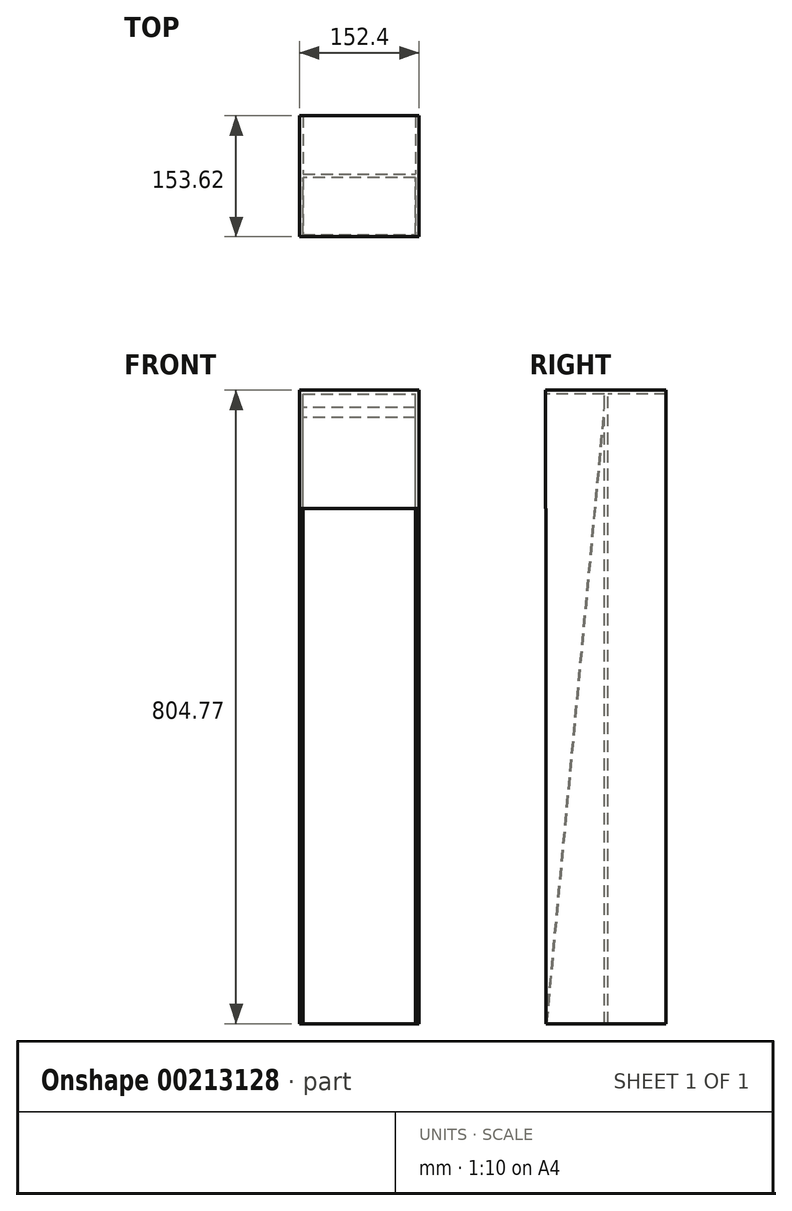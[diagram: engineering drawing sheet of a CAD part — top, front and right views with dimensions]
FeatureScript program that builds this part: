
annotation { "Feature Type Name" : "Feature", "Feature Type Description" : "" }
export const myFeature = defineFeature(function(context is Context, id is Id, definition is map)
    precondition{}
    {
        {
            var Q0;
            Q0=qCreatedBy(makeId("Top.planeOp"),FACE);
            var sketch = newSketch(context, id + "F0", { "sketchPlane" : qUnion([Q0])});
            skLineSegment(sketch, "E0.bottom", {"start": v(-76.2, -76.2) * mm, "end": v(-71.44, -76.2) * mm});
            skLineSegment(sketch, "E0.top", {"start": v(-76.2, 76.2) * mm, "end": v(-71.44, 76.2) * mm});
            skPoint(sketch, "E0.middle", {"position": v(0, 0) * mm});
            skLineSegment(sketch, "E1", {"start": v(-76.2, 76.2) * mm, "end": v(-76.2, -76.2) * mm});
            skLineSegment(sketch, "E2", {"start": v(-71.44, 76.2) * mm, "end": v(-71.44, 2.38) * mm});
            skLineSegment(sketch, "E3", {"start": v(76.2, 76.2) * mm, "end": v(76.2, -76.2) * mm});
            skLineSegment(sketch, "E4", {"start": v(71.44, 76.2) * mm, "end": v(71.44, 2.38) * mm});
            skLineSegment(sketch, "E5.trimOffspring", {"start": v(71.44, 76.2) * mm, "end": v(76.2, 76.2) * mm});
            skLineSegment(sketch, "E6.trimOffspring", {"start": v(71.44, -76.2) * mm, "end": v(76.2, -76.2) * mm});
            skLineSegment(sketch, "E7.0", {"start": v(-71.44, -2.38) * mm, "end": v(71.44, -2.38) * mm});
            skLineSegment(sketch, "E8.0", {"start": v(-71.44, 2.38) * mm, "end": v(71.44, 2.38) * mm});
            skLineSegment(sketch, "E9.trimOffspring", {"start": v(-71.44, -2.38) * mm, "end": v(-71.44, -76.2) * mm});
            skPoint(sketch, "E10.orphan", {"position": v(-71.44, 0) * mm});
            skPoint(sketch, "E11.end.orphan", {"position": v(71.44, 0) * mm});
            skLineSegment(sketch, "E12.trimOffspring", {"start": v(71.44, -2.38) * mm, "end": v(71.44, -76.2) * mm});
            skSolve(sketch);
        }
        {
            var Q0;
            Q0=qSketchRegion(id+"F0",true);
            extrude(context, id + "F1", {"entities" : qUnion([Q0]), "oppositeDirection" : true, "depth" : 800 * mm});
        }
        {
            var Q0;
            Q0=makeQuery(id+"F1.opExtrude","CAP_FACE",FACE,{"disambiguationData":[OSD([sQuery(id+"F0.wireOp",EDGE,"E0.bottom"),sQuery(id+"F0.wireOp",EDGE,"E0.top"),sQuery(id+"F0.wireOp",EDGE,"E0.left"),sQuery(id+"F0.wireOp",EDGE,"E0.right"),sQuery(id+"F0.wireOp",EDGE,"7a6f2c26-1c94-48de-b3ff-05aa15f8282d.0"),sQuery(id+"F0.wireOp",EDGE,"bf20579e-0ff9-4312-8226-057ec2ad24a0.0"),sQuery(id+"F0.wireOp",EDGE,"53fb2d3c-9874-4836-9c0b-58f450f03ea0.0"),sQuery(id+"F0.wireOp",EDGE,"893a7bcd-cfe5-4227-b07f-b4167a1dcdd1.0"),sQuery(id+"F0.wireOp",EDGE,"a6ffb2dd-69a9-4642-a933-3686e417fbb3.trimOffspring"),sQuery(id+"F0.wireOp",EDGE,"427ace22-e381-4167-ab2c-954d83dae6c8.trimOffspring"),sQuery(id+"F0.wireOp",EDGE,"ff942871-ae62-4c67-9aaa-94336091cfaf.trimOffspring"),sQuery(id+"F0.wireOp",EDGE,"886b6b8d-e2b2-4d8e-b841-3db4b76343a9.trimOffspring")])],"isStart":true});
            var sketch = newSketch(context, id + "F2", { "sketchPlane" : qUnion([Q0])});
            skLineSegment(sketch, "E13.bottom", {"start": v(-76.2, 76.2) * mm, "end": v(76.2, 76.2) * mm});
            skLineSegment(sketch, "E13.top", {"start": v(-76.2, -76.2) * mm, "end": v(76.2, -76.2) * mm});
            skLineSegment(sketch, "E13.left", {"start": v(-76.2, 76.2) * mm, "end": v(-76.2, -76.2) * mm});
            skLineSegment(sketch, "E13.right", {"start": v(76.2, 76.2) * mm, "end": v(76.2, -76.2) * mm});
            skPoint(sketch, "E13.middle", {"position": v(0, 0) * mm});
            skSolve(sketch);
        }
        {
            var Q0;
            Q0=qSketchRegion(id+"F2",true);
            extrude(context, id + "F3", {"entities" : qUnion([Q0]), "operationType" : NewBodyOperationType.ADD, "depth" : 4.76 * mm});
        }
        {
            var Q0;
            Q0=makeQuery(id+"F3.boolean.opBoolean","MERGE",FACE,{"derivedFrom":[makeQuery(id+"F1.opExtrude","SWEPT_FACE",FACE,{"disambiguationData":[OSD([sQuery(id+"F0.wireOp",EDGE,"E0.top")])]}),makeQuery(id+"F1.opExtrude","SWEPT_FACE",FACE,{"disambiguationData":[OSD([sQuery(id+"F0.wireOp",EDGE,"E5.trimOffspring")])]}),makeQuery(id+"F3.opExtrude","SWEPT_FACE",FACE,{"disambiguationData":[OSD([sQuery(id+"F2.wireOp",EDGE,"E13.bottom")])]})]});
            var sketch = newSketch(context, id + "F4", { "sketchPlane" : qUnion([Q0])});
            skLineSegment(sketch, "E14.top", {"start": v(-76.12, -3000.56) * mm, "end": v(75.55, -3000.56) * mm});
            skLineSegment(sketch, "E15", {"start": v(-76.2, -800) * mm, "end": v(76.2, -800) * mm});
            skLineSegment(sketch, "E16", {"start": v(-76.2, 4.76) * mm, "end": v(76.2, 4.76) * mm});
            skLineSegment(sketch, "E17", {"start": v(76.2, 4.76) * mm, "end": v(76.2, -800) * mm});
            skLineSegment(sketch, "E18", {"start": v(-76.2, -800) * mm, "end": v(-76.2, 4.76) * mm});
            skSolve(sketch);
        }
        {
            var Q0;
            Q0=qSketchRegion(id+"F4",true);
            extrude(context, id + "F5", {"entities" : qUnion([Q0]), "operationType" : NewBodyOperationType.ADD, "depth" : 3 / 406.4 * mm});
        }
        {
            var Q0;
            Q0=makeQuery(id+"F3.opExtrude","SWEPT_FACE",FACE,{"disambiguationData":[OSD([sQuery(id+"F2.wireOp",EDGE,"E13.top")])]});
            var sketch = newSketch(context, id + "F6", { "sketchPlane" : qUnion([Q0])});
            skLineSegment(sketch, "E19.bottom", {"start": v(-76.2, 4.76) * mm, "end": v(76.2, 4.76) * mm});
            skLineSegment(sketch, "E19.top", {"start": v(-76.2, -145.24) * mm, "end": v(76.2, -145.24) * mm});
            skLineSegment(sketch, "E19.left", {"start": v(-76.2, 4.76) * mm, "end": v(-76.2, -145.24) * mm});
            skLineSegment(sketch, "E19.right", {"start": v(76.2, 4.76) * mm, "end": v(76.2, -145.24) * mm});
            skSolve(sketch);
        }
        {
            var Q0;
            Q0=qSketchRegion(id+"F6",true);
            extrude(context, id + "F7", {"entities" : qUnion([Q0]), "operationType" : NewBodyOperationType.ADD, "depth" : 1.21 * mm});
        }
        {
            var Q0;
            Q0=qCreatedBy(makeId("Right.planeOp"),FACE);
            var sketch = newSketch(context, id + "F8", { "sketchPlane" : qUnion([Q0])});
            skPoint(sketch, "E20.start.orphan", {"position": v(0, 0) * mm});
            skLineSegment(sketch, "E21", {"start": v(0, 1698.73) * mm, "end": v(1.21, 1698.73) * mm});
            skLineSegment(sketch, "E22", {"start": v(-74.93, -800) * mm, "end": v(-76.14, -800) * mm});
            skLineSegment(sketch, "E23", {"start": v(-76.14, -800) * mm, "end": v(-0.32, 4.72) * mm});
            skLineSegment(sketch, "E24", {"start": v(-74.93, -800) * mm, "end": v(0.89, 4.72) * mm});
            skLineSegment(sketch, "E25", {"start": v(0.89, 4.72) * mm, "end": v(-0.32, 4.72) * mm});
            skPoint(sketch, "E26.orphan", {"position": v(0, 8.17) * mm});
            skSolve(sketch);
        }
        {
            var Q0;
            Q0=qSketchRegion(id+"F8",true);
            extrude(context, id + "F9", {"entities" : qUnion([Q0]), "operationType" : NewBodyOperationType.ADD, "endBound" : BoundingType.SYMMETRIC, "depth" : 152.4 * mm - 4.74 * mm - 4.74 * mm});
        }
    });
